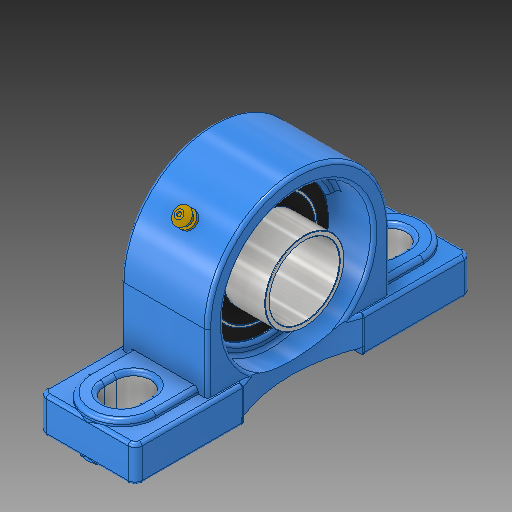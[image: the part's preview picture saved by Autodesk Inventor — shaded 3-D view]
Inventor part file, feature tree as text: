
AUTODESK INVENTOR PART (.ipt)
format: ipt  version: 2019 (Build 230136000, 136)  size: 681,984 bytes
history: native  units: in
note: dims shown in document units (in); Inventor stores cm internally (conversion verified against a paired STEP export)
features: sketch x28, plane x7, other x3
ambient origin geometry x8: Origin, YZ Plane, XZ Plane, XY Plane, X Axis, Y Axis, Z Axis, Center Point
bodies: Solid1 (feature_tree)
feature tree (38):
  other  "Pillow Bearing inventor_MIR_MIR1.ipt"
  other  "Solid1::Pillow Bearing inventor_MIR_MIR1.ipt"
  other  "TaggingFeature1"
  sketch  "Sketch1"  dims[d0=0.3937in]
  sketch  "Sketch2"
  sketch  "Sketch3"
  sketch  "Sketch4"
  sketch  "Sketch5"
  sketch  "Sketch6"
  sketch  "Sketch7"
  sketch  "Sketch8"
  sketch  "Sketch9"
  sketch  "Sketch10"
  sketch  "Sketch11"
  sketch  "Sketch13"
  sketch  "Sketch14"
  sketch  "Sketch15"
  sketch  "Sketch17"
  sketch  "Sketch18"
  sketch  "Sketch19"
  sketch  "Sketch20"
  sketch  "Sketch21"
  sketch  "Sketch22"
  sketch  "Sketch23"
  sketch  "Sketch24"
  sketch  "Sketch25"
  sketch  "Sketch26"
  sketch  "Sketch27"
  sketch  "Sketch28"
  sketch  "Sketch29"
  sketch  "Sketch30"
  plane  "Work Plane1"
  plane  "Work Plane2"
  plane  "Work Plane5"
  plane  "Work Plane6"
  plane  "Work Plane7"
  plane  "Work Plane8"
  plane  "Work Plane9"
